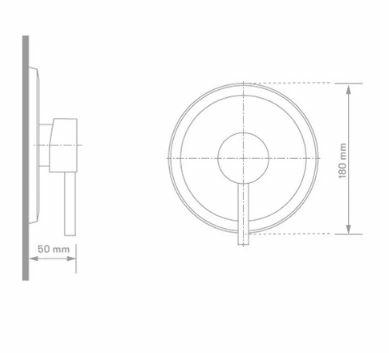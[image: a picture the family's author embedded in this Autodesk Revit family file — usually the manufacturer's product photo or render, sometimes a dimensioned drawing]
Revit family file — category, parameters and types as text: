
# Revit family: BL-2517-11-TOALLERO BARRA GENESIS
name_source: partatom
category: Plumbing Fixtures
revit_build: Autodesk Revit 2018 (Build: 20170223_1515(x64)
units: mm (PartAtom-declared; Revit-internal decimal feet)

## family parameters
Cut with Voids When Loaded = No
Host = Face
OmniClass Number = 23.31.11.00
Part Type = Normal
Room Calculation Point = No
Round Connector Dimension = Use Diameter
Shared = No

## types (1)
- BL-2517-11
    Alto = 50 mm  [stored 0.164042 ft]
    Ancho = 450 mm
    CW Connection = Yes
    Date Modified = BL-2517-11
    Default Elevation = 0 mm  [stored 0 ft]
    Description = TOALLERO
    Finish = Plastico ABS Cromado
    HW Connection = Yes
    Link Ficha Tecnica = http://infotecnica.gricol.com
    Manufacturer = Gricol
    Model = BL-2517-11
    Product Name = TOALLERO BARRA GENESIS
    Profundidad = 70 mm
    Type Image = TOALLERO BARRA.jpg
    URL = https://www.gricol.com
    Vent Connection = No
    Waste Connection = No

note: [stored X ft] marks values corroborated as IEEE doubles in the binary element streams (Revit-internal decimal feet)

## geometry (parser evidence)
native form markers: Blend x4, Sweep x4
no freeform markers — native parametric forms only
